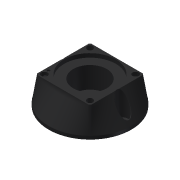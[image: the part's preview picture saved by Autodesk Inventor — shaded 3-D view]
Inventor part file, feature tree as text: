
AUTODESK INVENTOR PART (.ipt)
format: ipt  version: 2015 (Build 190159000, 159)  size: 960,000 bytes
history: native  units: in
note: dims shown in document units (in); Inventor stores cm internally (conversion verified against a paired STEP export)
features: fillet x1, other x1, extrude x1, imported_body x1, sketch x1
ambient origin geometry x8: Origin, YZ Plane, XZ Plane, XY Plane, X Axis, Y Axis, Z Axis, Center Point
bodies: Body1 (feature_tree)
feature tree (5):
  fillet  "Fillet3"  Radius=0.0394in
  other  "217-4018-STEP-201408061"
  extrude  "Extrusion1"  [1 undecoded]
  imported_body  "Base1"
  sketch  "Sketch1"
note: 1 required parameter value undecoded (feature->parameter linkage not recoverable at this tier; creation-order binding heuristic only, values carry confidence <= 0.55)
